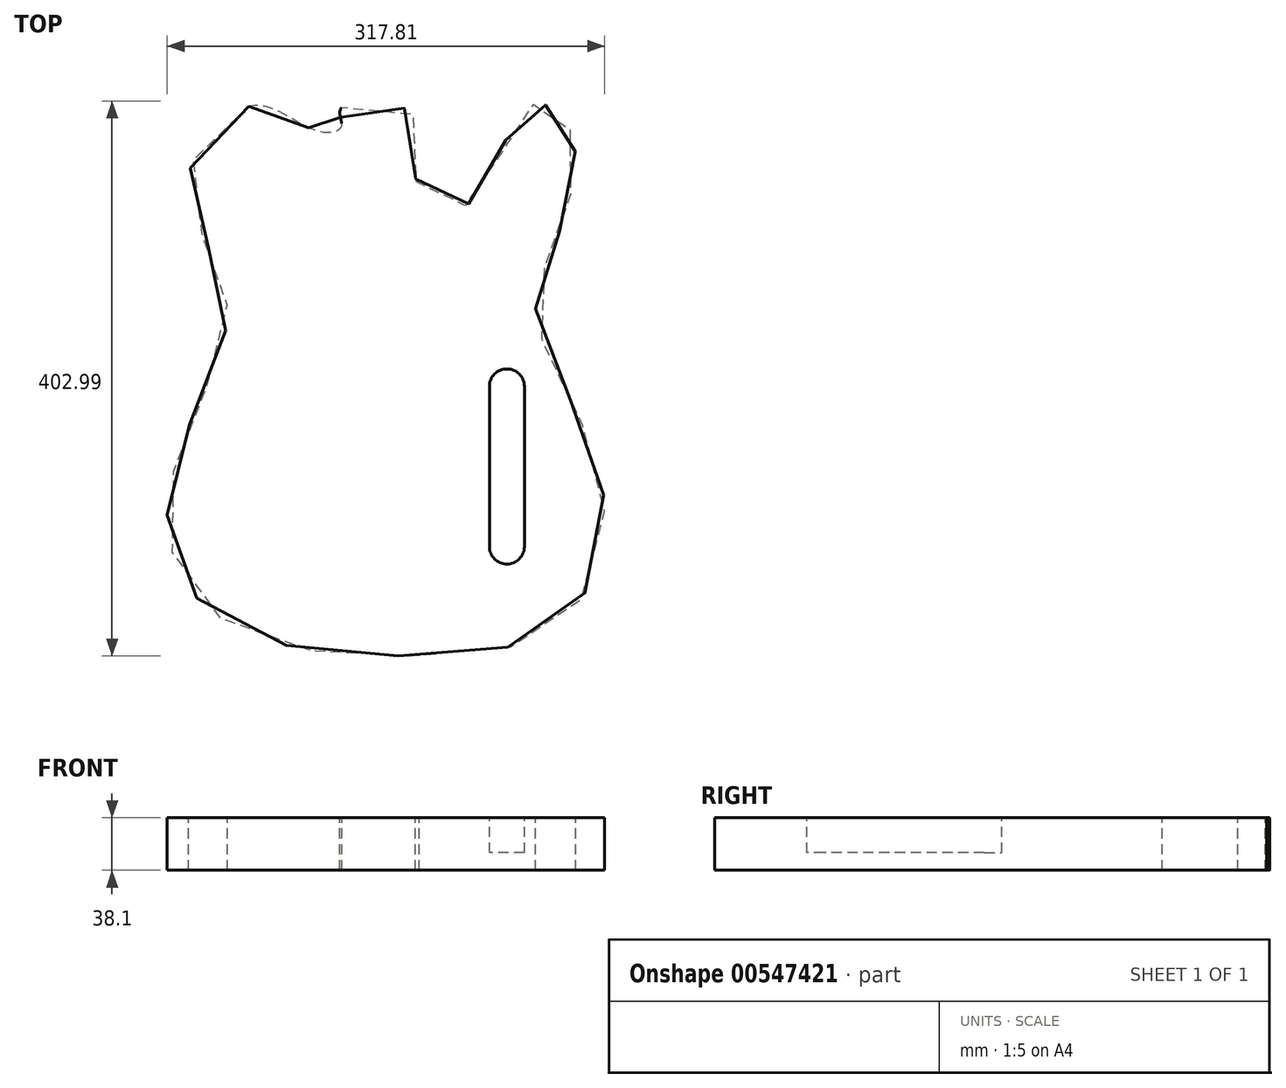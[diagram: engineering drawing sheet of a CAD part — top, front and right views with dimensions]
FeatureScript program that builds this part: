
annotation { "Feature Type Name" : "Feature", "Feature Type Description" : "" }
export const myFeature = defineFeature(function(context is Context, id is Id, definition is map)
    precondition{}
    {
        {
            var Q0;
            Q0=qCreatedBy(makeId("Top.planeOp"),FACE);
            var sketch = newSketch(context, id + "F0", { "sketchPlane" : qUnion([Q0])});
            skFitSpline(sketch, "E0", {"points": [v(-67.37, 168.18) * mm, v(-109.23, 125.44) * mm, v(-99.64, 71.36) * mm, v(-83.07, 15.53) * mm, v(-109.23, -60.35) * mm, v(-126.68, -129.26) * mm, v(-104.87, -189.45) * mm, v(-27.24, -226.08) * mm, v(76.56, -229.57) * mm, v(157.68, -208.64) * mm, v(190.82, -136.24) * mm, v(173.38, -59.48) * mm, v(141.1, 17.28) * mm, v(154.19, 67) * mm, v(169.89, 124.56) * mm, v(162.9, 156.84) * mm, v(144.6, 169.92) * mm, v(125.4, 158.58) * mm, v(108.83, 114.97) * mm, v(79.17, 94.04) * mm, v(53.88, 115.84) * mm, v(52.13, 162.07) * mm, v(0, 167.3) * mm, v(0, 154.22) * mm, v(-9.8, 148.99) * mm, v(-35.1, 158.58) * mm, v(-67.37, 168.18) * mm]});
            skArc(sketch, "E1", {"start": v(132.8, -35.2) * mm, "mid": v(120.1, -22.5) * mm, "end": v(107.4, -35.2) * mm});
            skArc(sketch, "E2", {"start": v(107.4, -151.5) * mm, "mid": v(120.1, -164.2) * mm, "end": v(132.8, -151.5) * mm});
            skLineSegment(sketch, "E3", {"start": v(107.4, -35.2) * mm, "end": v(107.4, -151.5) * mm});
            skLineSegment(sketch, "E4", {"start": v(132.8, -35.2) * mm, "end": v(132.8, -151.5) * mm});
            skFitSpline(sketch, "E5", {"points": [v(57.57, 81.1) * mm, v(-3.1, 80.44) * mm, v(-11.53, 76.22) * mm, v(-14.42, 69.78) * mm, v(-8.2, 60.67) * mm, v(17.57, 54.44) * mm, v(32.9, 54.44) * mm, v(62.01, 62.44) * mm, v(67.35, 70.67) * mm, v(65.12, 77.33) * mm, v(57.57, 81.1) * mm]});
            skArc(sketch, "E6", {"start": v(3.77, -29.92) * mm, "mid": v(-8.13, -36.22) * mm, "end": v(-1.83, -48.13) * mm});
            skArc(sketch, "E7", {"start": v(50.7, -64.28) * mm, "mid": v(62.6, -57.97) * mm, "end": v(56.3, -46.07) * mm});
            skLineSegment(sketch, "E8", {"start": v(3.77, -29.92) * mm, "end": v(56.3, -46.07) * mm});
            skLineSegment(sketch, "E9", {"start": v(-1.83, -48.13) * mm, "end": v(50.7, -64.28) * mm});
            skSolve(sketch);
        }
        {
            var Q0;
            Q0=makeQuery(id+"F0.imprint","IMPRINT",FACE,{"disambiguationData":[TD([[makeQuery(id+"F0.imprint","IMPRINT",EDGE,{"derivedFrom":sQuery(id+"F0.wireOp",EDGE,"E0")}),1.0]])]});
            var Q1;
            Q1=makeQuery(id+"F0.imprint","IMPRINT",FACE,{"disambiguationData":[TD([[makeQuery(id+"F0.imprint","IMPRINT",EDGE,{"derivedFrom":sQuery(id+"F0.wireOp",EDGE,"E5")}),1.0]])]});
            var Q2;
            Q2=makeQuery(id+"F0.imprint","IMPRINT",FACE,{"disambiguationData":[TD([[makeQuery(id+"F0.imprint","IMPRINT",EDGE,{"derivedFrom":sQuery(id+"F0.wireOp",EDGE,"E1")}),1.0]])]});
            var Q3;
            Q3=makeQuery(id+"F0.imprint","IMPRINT",FACE,{"disambiguationData":[TD([[makeQuery(id+"F0.imprint","IMPRINT",EDGE,{"derivedFrom":sQuery(id+"F0.wireOp",EDGE,"E6")}),1.0]])]});
            extrude(context, id + "F1", {"entities" : qUnion([Q0, Q1, Q2, Q3]), "oppositeDirection" : true, "depth" : 38.1 * mm, "offsetDistance" : 25.4 * mm});
        }
        {
            var Q0;
            Q0=makeQuery(id+"F0.imprint","IMPRINT",FACE,{"disambiguationData":[TD([[makeQuery(id+"F0.imprint","IMPRINT",EDGE,{"derivedFrom":sQuery(id+"F0.wireOp",EDGE,"E1")}),1.0]])]});
            extrude(context, id + "F2", {"entities" : qUnion([Q0]), "operationType" : NewBodyOperationType.REMOVE, "oppositeDirection" : true, "depth" : 25.4 * mm, "offsetDistance" : 25.4 * mm});
        }
    });
